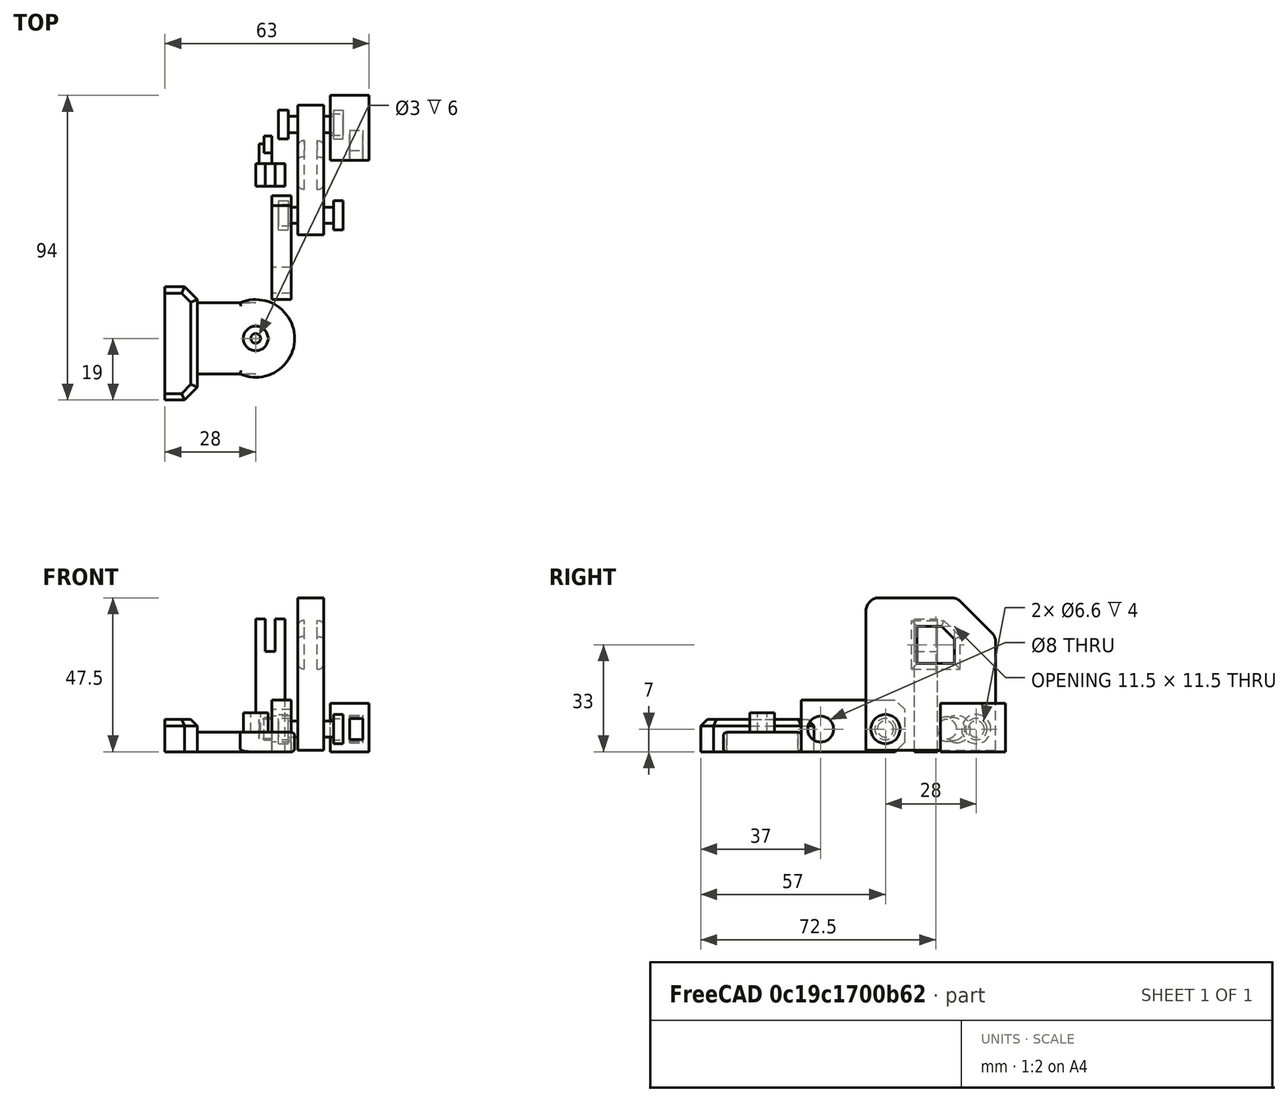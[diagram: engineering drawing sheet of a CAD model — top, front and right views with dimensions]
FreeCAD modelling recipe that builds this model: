
FCSTD DOCUMENT  (FreeCAD 0.18R16117 (Git))
Label: SD-Mech
License: All rights reserved
LicenseURL: http://en.wikipedia.org/wiki/All_rights_reserved
objects: Part::Cylinder×18, Part::Box×8, Part::Cut×8, Part::MultiFuse×8, Part::Chamfer×5, Part::Fillet×4, Part::Mirroring×4, Part::Plane×1
note: 56 computed .brp shape members not serialized (recipe doc carries the construction recipe); baked Part::Feature solids carry a one-line shape summary decoded from their .brp

FEATURE [Part::Plane] Plane
  AttacherType = Attacher::AttachEngine3D
  Length = 100
  Placement = pos=(-50,-50,-1) rot=(0,0,1;0rad)
  Width = 100
FEATURE [Part::Box] Box  label="Cube"
  AttacherType = Attacher::AttachEngine3D
  Height = 47
  Length = 8
  Placement = pos=(-4,5,0.5) rot=(0,0,1;0rad)
  Width = 40
FEATURE [Part::Chamfer] Chamfer
  Base = -> Box
  Edges = 1 edges r=12: [Edge12]
FEATURE [Part::Fillet] Fillet
  Base = -> Chamfer
  Edges = 3 edges r=4: [Edge6,Edge7,Edge9]
FEATURE [Part::Box] Box001  label="Cube001"
  AttacherType = Attacher::AttachEngine3D
  Height = 15
  Length = 2
  Placement = pos=(0,0,0.5) rot=(0,0,1;0rad)
  Width = 15
FEATURE [Part::Chamfer] Chamfer001
  Base = -> Box001
  Edges = 1 edges r=5: [Edge12]
FEATURE [Part::Fillet] Fillet001
  Base = -> Chamfer001
  Edges = 5 edges r=1.75: [Edge8,Edge10,Edge12,Edge13,Edge15]
  Placement = pos=(2,19,25) rot=(0,0,1;0rad)
FEATURE [Part::Mirroring] Part__Mirroring  label="Fillet001 (Mirror #1)"
  Base = (0,0,0)
  Normal = (1,0,0)
  Source = -> Fillet001
FEATURE [Part::Cut] Cut
  Base = -> Fillet
  Tool = -> Fillet001
FEATURE [Part::Cut] Cut001
  Base = -> Cut
  Tool = -> Part__Mirroring
FEATURE [Part::Cylinder] Cylinder
  Angle = 360
  AttacherType = Attacher::AttachEngine3D
  Height = 20
  Placement = pos=(-10,11,7) rot=(0,1,0;1.5708rad)
  Radius = 2.5
FEATURE [Part::Cylinder] Cylinder001
  Angle = 360
  AttacherType = Attacher::AttachEngine3D
  Height = 3
  Placement = pos=(-10,11,7) rot=(0,1,0;1.5708rad)
  Radius = 4.5
FEATURE [Part::Cylinder] Cylinder002
  Angle = 360
  AttacherType = Attacher::AttachEngine3D
  Height = 3
  Placement = pos=(7,11,7) rot=(0,1,0;1.5708rad)
  Radius = 4.5
FEATURE [Part::Cylinder] Cylinder003
  Angle = 360
  AttacherType = Attacher::AttachEngine3D
  Height = 20
  Placement = pos=(-10,11,7) rot=(0,1,0;1.5708rad)
  Radius = 3.3
FEATURE [Part::Cylinder] Cylinder004
  Angle = 360
  AttacherType = Attacher::AttachEngine3D
  Height = 4
  Placement = pos=(-10,11,7) rot=(0,1,0;1.5708rad)
  Radius = 5.3
FEATURE [Part::MultiFuse] Fusion
  Shapes = -> [Cylinder,Cylinder001,Cylinder002]
FEATURE [Part::MultiFuse] Fusion001
  Shapes = -> [Cylinder003,Cylinder004]
FEATURE [Part::Cylinder] Cylinder005
  Angle = 360
  AttacherType = Attacher::AttachEngine3D
  Height = 20
  Placement = pos=(-10,11,7) rot=(0,1,0;1.5708rad)
  Radius = 2.5
FEATURE [Part::Cylinder] Cylinder006
  Angle = 360
  AttacherType = Attacher::AttachEngine3D
  Height = 4
  Placement = pos=(-10,11,7) rot=(0,1,0;1.5708rad)
  Radius = 5.3
FEATURE [Part::Cylinder] Cylinder007
  Angle = 360
  AttacherType = Attacher::AttachEngine3D
  Height = 20
  Placement = pos=(-10,11,7) rot=(0,1,0;1.5708rad)
  Radius = 3.3
FEATURE [Part::MultiFuse] Fusion003
  Placement = pos=(0,28,0) rot=(0,0,1;0rad)
  Shapes = -> [Cylinder007,Cylinder006]
FEATURE [Part::Cylinder] Cylinder008
  Angle = 360
  AttacherType = Attacher::AttachEngine3D
  Height = 3
  Placement = pos=(7,11,7) rot=(0,1,0;1.5708rad)
  Radius = 4.5
FEATURE [Part::Cylinder] Cylinder009
  Angle = 360
  AttacherType = Attacher::AttachEngine3D
  Height = 3
  Placement = pos=(-10,11,7) rot=(0,1,0;1.5708rad)
  Radius = 4.5
FEATURE [Part::MultiFuse] Fusion002
  Placement = pos=(0,28,0) rot=(0,0,1;0rad)
  Shapes = -> [Cylinder005,Cylinder009,Cylinder008]
FEATURE [Part::MultiFuse] Fusion004
  Shapes = -> [Cut001,Fusion,Fusion002]
FEATURE [Part::Box] Box002  label="Cube002"
  AttacherType = Attacher::AttachEngine3D
  Height = 16
  Length = 6
  Placement = pos=(6,-15,0) rot=(0,0,1;0rad)
  Width = 32
FEATURE [Part::Box] Box003  label="Cube003"
  AttacherType = Attacher::AttachEngine3D
  Height = 15
  Length = 12
  Placement = pos=(6,28,0) rot=(0,0,1;0rad)
  Width = 20
FEATURE [Part::Box] Box004  label="Cube004"
  AttacherType = Attacher::AttachEngine3D
  Height = 41
  Length = 9
  Placement = pos=(8,20,0) rot=(0,0,1;0rad)
  Width = 7
FEATURE [Part::Box] Box005  label="Cube005"
  AttacherType = Attacher::AttachEngine3D
  Height = 10
  Length = 3
  Placement = pos=(11,20,31) rot=(0,0,1;0rad)
  Width = 7
FEATURE [Part::Cut] Cut002
  Base = -> Box004
  Tool = -> Box005
FEATURE [Part::Cut] Cut003
  Base = -> Box003
  Tool = -> Fusion003
FEATURE [Part::Chamfer] Chamfer002
  Base = -> Box002
  Edges = 2 edges r=3: [Edge11,Edge12]
FEATURE [Part::Cut] Cut004
  Base = -> Chamfer002
  Tool = -> Fusion001
FEATURE [Part::Cylinder] Cylinder010
  Angle = 360
  AttacherType = Attacher::AttachEngine3D
  Height = 20
  Placement = pos=(0,-9,7) rot=(0,1,0;1.5708rad)
  Radius = 4
FEATURE [Part::Cut] Cut005
  Base = -> Cut004
  Tool = -> Cylinder010
FEATURE [Part::Mirroring] Part__Mirroring001  label="Cut005 (Mirror #2)"
  Base = (0,0,0)
  Normal = (1,0,0)
  Source = -> Cut005
FEATURE [Part::Cylinder] Cylinder011
  Angle = 360
  AttacherType = Attacher::AttachEngine3D
  Height = 4
  Placement = pos=(12,30,7) rot=(0,1,0;1.5708rad)
  Radius = 3
FEATURE [Part::Cylinder] Cylinder012
  Angle = 360
  AttacherType = Attacher::AttachEngine3D
  Height = 2.5
  Placement = pos=(12,32,7) rot=(0,1,0;1.5708rad)
  Radius = 3.5
FEATURE [Part::Cylinder] Cylinder013
  Angle = 360
  AttacherType = Attacher::AttachEngine3D
  Height = 4
  Placement = pos=(12,30,7) rot=(0,1,0;1.5708rad)
  Radius = 3.8
FEATURE [Part::Cylinder] Cylinder014
  Angle = 360
  AttacherType = Attacher::AttachEngine3D
  Height = 4
  Placement = pos=(12,33,7) rot=(0,1,0;1.5708rad)
  Radius = 4.2
FEATURE [Part::MultiFuse] Fusion005
  Shapes = -> [Cylinder013,Cylinder014]
FEATURE [Part::Cut] Cut006
  Base = -> Cut003
  Tool = -> Fusion005
FEATURE [Part::MultiFuse] Fusion006
  Shapes = -> [Cut002,Cylinder011,Cylinder012]
FEATURE [Part::Mirroring] Part__Mirroring002  label="Fusion006 (Mirror #3)"
  Base = (0,0,0)
  Normal = (1,0,0)
  Source = -> Fusion006
FEATURE [Part::Cylinder] Cylinder015
  Angle = 360
  AttacherType = Attacher::AttachEngine3D
  Height = 6
  Placement = pos=(17,-27,0) rot=(0,0,1;0rad)
  Radius = 12
FEATURE [Part::Cylinder] Cylinder016
  Angle = 360
  AttacherType = Attacher::AttachEngine3D
  Height = 6
  Placement = pos=(17,-27,6) rot=(0,0,1;0rad)
  Radius = 3.8
FEATURE [Part::Cylinder] Cylinder017
  Angle = 360
  AttacherType = Attacher::AttachEngine3D
  Height = 6
  Placement = pos=(17,-27,6) rot=(0,0,1;0rad)
  Radius = 1.5
FEATURE [Part::Cut] Cut007
  Base = -> Cylinder016
  Tool = -> Cylinder017
FEATURE [Part::Fillet] Fillet002
  Base = -> Cylinder015
  Edges = 2 edges r=1: [Edge1,Edge3]
FEATURE [Part::Box] Box006  label="Cube006"
  AttacherType = Attacher::AttachEngine3D
  Height = 6
  Length = 21
  Placement = pos=(17,-38,0) rot=(0,0,1;0rad)
  Width = 22
FEATURE [Part::Box] Box007  label="Cube007"
  AttacherType = Attacher::AttachEngine3D
  Height = 10
  Length = 10
  Placement = pos=(35,-46,0) rot=(0,0,1;0rad)
  Width = 35
FEATURE [Part::Fillet] Fillet003
  Base = -> Box006
  Edges = 2 edges r=1: [Edge10,Edge12]
FEATURE [Part::Chamfer] Chamfer003
  Base = -> Box007
  Edges = 2 edges r=4: [Edge1,Edge3]
FEATURE [Part::Chamfer] Chamfer004
  Base = -> Chamfer003
  Edges = 5 edges r=2: [Edge1,Edge5,Edge6,Edge7,Edge8]
FEATURE [Part::MultiFuse] Fusion007
  Shapes = -> [Cut007,Fillet002,Fillet003,Chamfer004]
FEATURE [Part::Mirroring] Part__Mirroring003  label="Fusion007 (Mirror #4)"
  Base = (0,0,0)
  Normal = (1,0,0)
  Source = -> Fusion007
